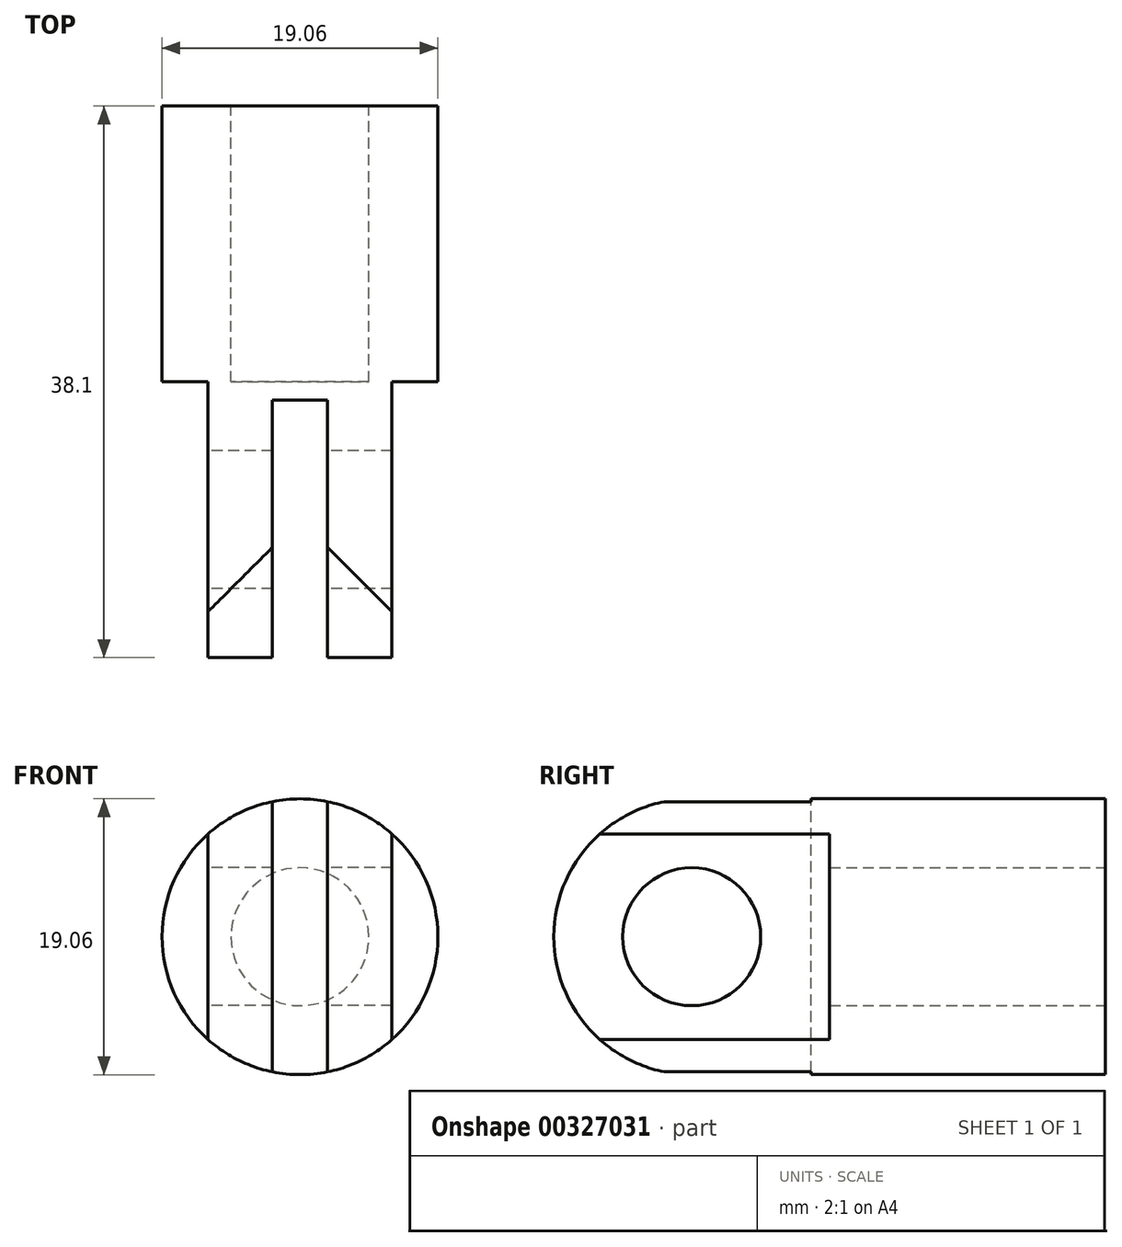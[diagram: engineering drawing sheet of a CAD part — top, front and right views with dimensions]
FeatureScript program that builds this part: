
annotation { "Feature Type Name" : "Feature", "Feature Type Description" : "" }
export const myFeature = defineFeature(function(context is Context, id is Id, definition is map)
    precondition{}
    {
        {
            var Q0;
            Q0=qCreatedBy(makeId("Front.planeOp"),FACE);
            var sketch = newSketch(context, id + "F0", { "sketchPlane" : qUnion([Q0])});
            skCircle(sketch, "E0", {"center": v(0, 0) * mm, "radius": 9.53 * mm});
            skCircle(sketch, "E1", {"center": v(0, 0) * mm, "radius": 4.76 * mm});
            skSolve(sketch);
        }
        {
            var Q0;
            Q0=makeQuery(id+"F0.imprint","IMPRINT",FACE,{"disambiguationData":[TD([[makeQuery(id+"F0.imprint","IMPRINT",EDGE,{"derivedFrom":sQuery(id+"F0.wireOp",EDGE,"E0")}),1.0]])]});
            extrude(context, id + "F1", {"entities" : qUnion([Q0]), "depth" : 19.05 * mm});
        }
        {
            var Q0;
            Q0=makeQuery(id+"F1.opExtrude","CAP_FACE",FACE,{"disambiguationData":[OSD([sQuery(id+"F0.wireOp",EDGE,"E0"),sQuery(id+"F0.wireOp",EDGE,"E1")])],"isStart":false});
            var sketch = newSketch(context, id + "F2", { "sketchPlane" : qUnion([Q0])});
            skArc(sketch, "E2", {"start": v(-6.35, -7.1) * mm, "mid": v(0, -9.53) * mm, "end": v(6.35, -7.1) * mm});
            skLineSegment(sketch, "E3", {"start": v(-6.35, 7.1) * mm, "end": v(-6.35, -7.1) * mm});
            skLineSegment(sketch, "E4", {"start": v(6.35, 7.1) * mm, "end": v(6.35, -7.1) * mm});
            skArc(sketch, "E5.trimOffspring", {"start": v(6.35, 7.1) * mm, "mid": v(0, 9.52) * mm, "end": v(-6.35, 7.1) * mm});
            skSolve(sketch);
        }
        {
            var Q0;
            Q0 = qSketchRegion(id + "F2", true);
            extrude(context, id + "F3", {"entities" : qUnion([Q0]), "operationType" : NewBodyOperationType.ADD, "depth" : 19.05 * mm});
        }
        {
            var Q0;
            Q0=makeQuery(id+"F3.opExtrude","SWEPT_FACE",FACE,{"disambiguationData":[OSD([sQuery(id+"F2.wireOp",EDGE,"E3")])]});
            var sketch = newSketch(context, id + "F4", { "sketchPlane" : qUnion([Q0])});
            skCircle(sketch, "E6", {"center": v(28.58, 0) * mm, "radius": 4.76 * mm});
            skSolve(sketch);
        }
        {
            var Q0;
            Q0=makeQuery(id+"F4.imprint","IMPRINT",FACE,{"disambiguationData":[TD([[makeQuery(id+"F4.imprint","IMPRINT",EDGE,{"derivedFrom":sQuery(id+"F4.wireOp",EDGE,"E6")}),1.0]])]});
            extrude(context, id + "F5", {"entities" : qUnion([Q0]), "operationType" : NewBodyOperationType.REMOVE, "endBound" : BoundingType.THROUGH_ALL, "oppositeDirection" : true, "depth" : 25.4 * mm});
        }
        {
            var Q0;
            Q0=makeQuery(id+"F3.opExtrude","SWEPT_FACE",FACE,{"disambiguationData":[OSD([sQuery(id+"F2.wireOp",EDGE,"E4")])]});
            var sketch = newSketch(context, id + "F6", { "sketchPlane" : qUnion([Q0])});
            skArc(sketch, "E7", {"start": v(-28.85, 9.52) * mm, "mid": v(-38.1, 0) * mm, "end": v(-28.85, -9.52) * mm});
            skLineSegment(sketch, "E8.right", {"start": v(-38.74, 9.52) * mm, "end": v(-38.74, -9.52) * mm});
            skLineSegment(sketch, "E9", {"start": v(-28.85, 9.52) * mm, "end": v(-28.85, 11.03) * mm});
            skLineSegment(sketch, "E10", {"start": v(-28.85, 11.03) * mm, "end": v(-38.74, 11.03) * mm});
            skLineSegment(sketch, "E11", {"start": v(-38.74, 11.03) * mm, "end": v(-38.74, 9.52) * mm});
            skLineSegment(sketch, "E12", {"start": v(-28.85, -9.52) * mm, "end": v(-28.85, -10.82) * mm});
            skLineSegment(sketch, "E13", {"start": v(-28.85, -10.82) * mm, "end": v(-38.74, -10.82) * mm});
            skLineSegment(sketch, "E14", {"start": v(-38.74, -10.82) * mm, "end": v(-38.74, -9.52) * mm});
            skSolve(sketch);
        }
        {
            var Q0;
            Q0 = qSketchRegion(id + "F6", true);
            extrude(context, id + "F7", {"entities" : qUnion([Q0]), "operationType" : NewBodyOperationType.REMOVE, "endBound" : BoundingType.THROUGH_ALL, "oppositeDirection" : true, "depth" : 25.4 * mm});
        }
        {
            var Q0;
            Q0=qCreatedBy(makeId("Top.planeOp"),FACE);
            var sketch = newSketch(context, id + "F8", { "sketchPlane" : qUnion([Q0])});
            skLineSegment(sketch, "E15.bottom", {"start": v(-1.9, -40.64) * mm, "end": v(1.9, -40.64) * mm});
            skLineSegment(sketch, "E15.top", {"start": v(-1.9, -20.32) * mm, "end": v(1.9, -20.32) * mm});
            skLineSegment(sketch, "E15.left", {"start": v(-1.9, -40.64) * mm, "end": v(-1.9, -20.32) * mm});
            skLineSegment(sketch, "E15.right", {"start": v(1.9, -40.64) * mm, "end": v(1.9, -20.32) * mm});
            skSolve(sketch);
        }
        {
            var Q0;
            Q0 = qSketchRegion(id + "F8", true);
            extrude(context, id + "F9", {"entities" : qUnion([Q0]), "operationType" : NewBodyOperationType.REMOVE, "endBound" : BoundingType.THROUGH_ALL, "oppositeDirection" : true, "depth" : 25.4 * mm});
        }
        {
            var Q0;
            Q0 = qSketchRegion(id + "F8", true);
            extrude(context, id + "F10", {"entities" : qUnion([Q0]), "operationType" : NewBodyOperationType.REMOVE, "endBound" : BoundingType.THROUGH_ALL, "depth" : 25.4 * mm});
        }
    });
